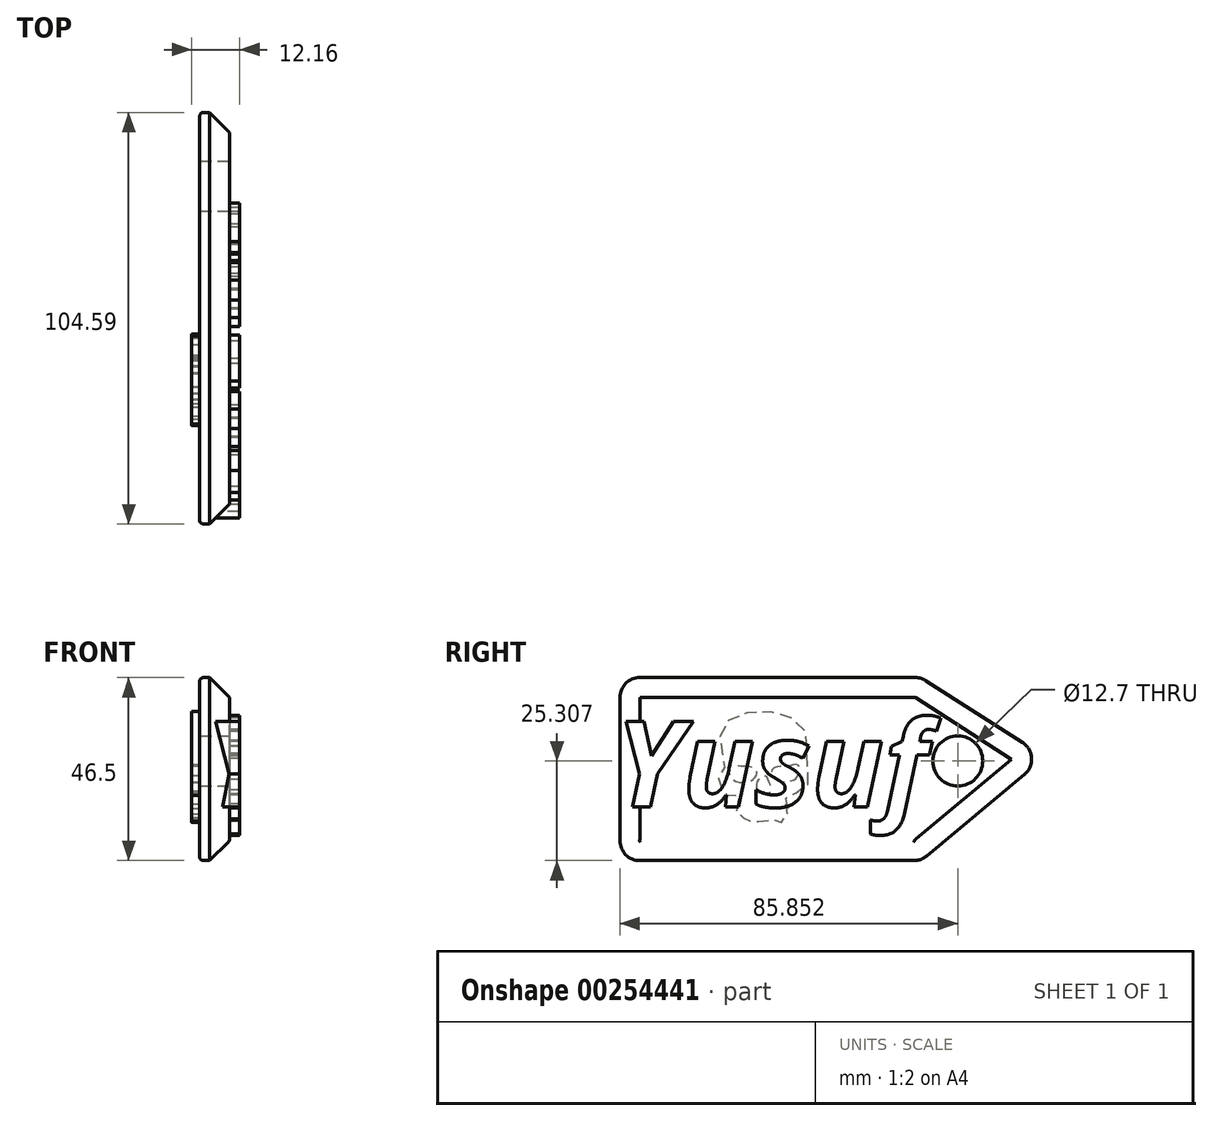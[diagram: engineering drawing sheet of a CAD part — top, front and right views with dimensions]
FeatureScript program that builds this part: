
annotation { "Feature Type Name" : "Feature", "Feature Type Description" : "" }
export const myFeature = defineFeature(function(context is Context, id is Id, definition is map)
    precondition{}
    {
        {
            var Q0;
            Q0=qCreatedBy(makeId("Right.planeOp"),FACE);
            cPlane(context, id + "F0", {"entities" : qUnion([Q0]), "cplaneType" : CPlaneType.OFFSET, "offset" : 25.4 * mm, "width" : 152.4 * mm, "height" : 152.4 * mm});
        }
        {
            var Q0;
            Q0=qCreatedBy(id+"F0.planeOp",FACE);
            var sketch = newSketch(context, id + "F1", { "sketchPlane" : qUnion([Q0])});
            skLineSegment(sketch, "E0", {"start": v(-76.54, 56) * mm, "end": v(-76.54, 9.51) * mm});
            skLineSegment(sketch, "E1", {"start": v(-76.54, 9.51) * mm, "end": v(0, 9.51) * mm});
            skLineSegment(sketch, "E2", {"start": v(-76.54, 56) * mm, "end": v(0, 56) * mm});
            skLineSegment(sketch, "E3", {"start": v(0, 56) * mm, "end": v(0, 9.51) * mm});
            skLineSegment(sketch, "E4", {"start": v(0, 56) * mm, "end": v(31.55, 35.78) * mm});
            skLineSegment(sketch, "E5", {"start": v(31.55, 35.78) * mm, "end": v(0, 9.51) * mm});
            skSolve(sketch);
        }
        {
            var Q0;
            Q0=makeQuery(id+"F1.imprint","IMPRINT",FACE,{"disambiguationData":[TD([[makeQuery(id+"F1.imprint","IMPRINT",EDGE,{"derivedFrom":sQuery(id+"F1.wireOp",EDGE,"E0")}),1.0]])]});
            var Q1;
            Q1=makeQuery(id+"F1.imprint","IMPRINT",FACE,{"disambiguationData":[TD([[makeQuery(id+"F1.imprint","IMPRINT",EDGE,{"derivedFrom":sQuery(id+"F1.wireOp",EDGE,"E3")}),1.0]])]});
            extrude(context, id + "F2", {"entities" : qUnion([Q0, Q1]), "depth" : 7.62 * mm});
        }
        {
            var Q0;
            Q0=makeQuery(id+"F2.opExtrude","CAP_FACE",FACE,{"disambiguationData":[OSD([sQuery(id+"F1.wireOp",EDGE,"E0"),sQuery(id+"F1.wireOp",EDGE,"E1"),sQuery(id+"F1.wireOp",EDGE,"E2"),sQuery(id+"F1.wireOp",EDGE,"E4"),sQuery(id+"F1.wireOp",EDGE,"E5")])],"isStart":false});
            var sketch = newSketch(context, id + "F3", { "sketchPlane" : qUnion([Q0])});
            skPoint(sketch, "E6", {"position": v(9.31, 34.82) * mm});
            skCircle(sketch, "E7", {"center": v(9.31, 34.82) * mm, "radius": 5.77 * mm});
            skSolve(sketch);
        }
        {
            var Q0;
            Q0=sQuery(id+"F3.wireOp",VERTEX,"E6");
            var Q1;
            Q1=makeQuery(id+"F2.opExtrude","SWEPT_BODY",BODY,{"disambiguationData":[OSD([sQuery(id+"F1.wireOp",EDGE,"E0"),sQuery(id+"F1.wireOp",EDGE,"E1"),sQuery(id+"F1.wireOp",EDGE,"E2"),sQuery(id+"F1.wireOp",EDGE,"E4"),sQuery(id+"F1.wireOp",EDGE,"E5")])]});
            hole(context, id + "F4", {"style" : HoleStyle.SIMPLE, "endStyle" : HoleEndStyle.BLIND, "holeDiameter" : 12.7 * mm, "holeDepth" : 25.4 * mm, "tappedDepth" : 12.7 * mm, "tapClearance" : 3, "locations" : qUnion([Q0]), "scope" : qUnion([Q1])});
        }
        {
            var Q0;
            Q0=makeQuery(id+"F2.opExtrude","SWEPT_EDGE",EDGE,{"disambiguationData":[OSD([sQuery(id+"F1.wireOp",EDGE,"E4"),sQuery(id+"F1.wireOp",EDGE,"E5")])]});
            fillet(context, id + "F5", {"entities" : qUnion([Q0]), "radius" : 5.08 * mm, "tangentPropagation" : true, "allowEdgeOverflow" : false});
        }
        {
            var Q0;
            Q0=makeQuery(id+"F2.opExtrude","SWEPT_EDGE",EDGE,{"disambiguationData":[OSD([sQuery(id+"F1.wireOp",EDGE,"E2"),sQuery(id+"F1.wireOp",EDGE,"E3"),sQuery(id+"F1.wireOp",EDGE,"E4")])]});
            fillet(context, id + "F6", {"entities" : qUnion([Q0]), "radius" : 5.08 * mm, "tangentPropagation" : true, "allowEdgeOverflow" : false});
        }
        {
            var Q0;
            Q0=makeQuery(id+"F2.opExtrude","SWEPT_EDGE",EDGE,{"disambiguationData":[OSD([sQuery(id+"F1.wireOp",EDGE,"E0"),sQuery(id+"F1.wireOp",EDGE,"E2")])]});
            fillet(context, id + "F7", {"entities" : qUnion([Q0]), "radius" : 5.08 * mm, "tangentPropagation" : true, "allowEdgeOverflow" : false});
        }
        {
            var Q0;
            Q0=makeQuery(id+"F2.opExtrude","SWEPT_EDGE",EDGE,{"disambiguationData":[OSD([sQuery(id+"F1.wireOp",EDGE,"E0"),sQuery(id+"F1.wireOp",EDGE,"E1")])]});
            var Q1;
            Q1=makeQuery(id+"F2.opExtrude","SWEPT_EDGE",EDGE,{"disambiguationData":[OSD([sQuery(id+"F1.wireOp",EDGE,"E1"),sQuery(id+"F1.wireOp",EDGE,"E3"),sQuery(id+"F1.wireOp",EDGE,"E5")])]});
            fillet(context, id + "F8", {"entities" : qUnion([Q0, Q1]), "radius" : 5.08 * mm, "tangentPropagation" : true, "allowEdgeOverflow" : false});
        }
        {
            var Q0;
            Q0=makeQuery(id+"F2.opExtrude","CAP_FACE",FACE,{"disambiguationData":[OSD([sQuery(id+"F1.wireOp",EDGE,"E0"),sQuery(id+"F1.wireOp",EDGE,"E1"),sQuery(id+"F1.wireOp",EDGE,"E2"),sQuery(id+"F1.wireOp",EDGE,"E4"),sQuery(id+"F1.wireOp",EDGE,"E5")])],"isStart":false});
            var sketch = newSketch(context, id + "F9", { "sketchPlane" : qUnion([Q0])});
            skText(sketch, "E8", { "text": "Yusuf", "fontName": "OpenSans-BoldItalic.ttf"});
            const initialGuessF9  = {"E8": [-0.0778, 0.02318, 1, 0, 0.02187]};
            skSetInitialGuess(sketch, initialGuessF9);
            skSolve(sketch);
        }
        {
            var Q0;
            Q0 = qSketchRegion(id + "F9", true);
            extrude(context, id + "F10", {"entities" : qUnion([Q0]), "operationType" : NewBodyOperationType.ADD, "depth" : 2.54 * mm});
        }
        {
            var Q0;
            Q0=makeQuery(id+"F2.opExtrude","CAP_EDGE",EDGE,{"disambiguationData":[OSD([sQuery(id+"F1.wireOp",EDGE,"E1")])],"isStart":false});
            chamfer(context, id + "F11", {"entities" : qUnion([Q0]), "width" : 5.08 * mm, "tangentPropagation" : true});
        }
        {
            var Q0;
            Q0=makeQuery(id+"F2.opExtrude","CAP_FACE",FACE,{"disambiguationData":[OSD([sQuery(id+"F1.wireOp",EDGE,"E0"),sQuery(id+"F1.wireOp",EDGE,"E1"),sQuery(id+"F1.wireOp",EDGE,"E2"),sQuery(id+"F1.wireOp",EDGE,"E4"),sQuery(id+"F1.wireOp",EDGE,"E5")])],"isStart":true});
            var sketch = newSketch(context, id + "F12", { "sketchPlane" : qUnion([Q0])});
            skFitSpline(sketch, "E9", {"points": [v(29.67, 42.78) * mm, v(31.96, 45.13) * mm, v(34.37, 46.34) * mm, v(37.68, 47.23) * mm, v(42.52, 47.36) * mm, v(45.83, 46.6) * mm, v(48.57, 45.38) * mm, v(50.13, 43.7) * mm, v(51.03, 41.36) * mm, v(50.8, 38.61) * mm, v(50.45, 36.23) * mm, v(50.31, 34.7) * mm, v(50, 33.98) * mm, v(50.18, 32.58) * mm, v(50.67, 31.95) * mm, v(51.44, 30.83) * mm, v(51.44, 29.16) * mm, v(50.54, 26.6) * mm, v(48.78, 26.06) * mm, v(46.8, 26.37) * mm, v(46.08, 25.6) * mm, v(46.17, 24.3) * mm, v(46.98, 21.78) * mm, v(46.62, 21.51) * mm, v(46.08, 21.1) * mm, v(45.27, 20.43) * mm, v(44.95, 20.25) * mm, v(45, 19.58) * mm, v(44.36, 19.44) * mm, v(43.42, 19.58) * mm, v(43.46, 19.98) * mm, v(42.42, 19.71) * mm, v(42.02, 19.53) * mm, v(39.86, 19.58) * mm, v(39.68, 19.71) * mm, v(37.74, 19.85) * mm, v(36.4, 20.34) * mm, v(36.62, 19.49) * mm, v(35.13, 19.35) * mm, v(35.09, 20.16) * mm, v(34.9, 20.61) * mm, v(34.05, 21.33) * mm, v(33.83, 21.74) * mm, v(33.83, 22.77) * mm, v(33.74, 23.5) * mm, v(34.1, 24.26) * mm, v(34.32, 25.16) * mm, v(34.23, 26.1) * mm, v(32.93, 27.05) * mm, v(31.44, 26.55) * mm, v(29.73, 27.32) * mm, v(28.7, 29.2) * mm, v(28.3, 31.23) * mm, v(28.88, 33.08) * mm, v(29.37, 34.11) * mm, v(28.97, 37.4) * mm, v(28.92, 41.18) * mm, v(29.67, 42.78) * mm]});
            skFitSpline(sketch, "E10", {"points": [v(31.13, 33.66) * mm, v(32.8, 33.75) * mm, v(34.28, 33.48) * mm, v(36.4, 33.35) * mm, v(37.88, 32.54) * mm, v(37.97, 31.46) * mm, v(37.11, 30.29) * mm, v(34.6, 29.48) * mm, v(32.07, 30.15) * mm, v(31.3, 31.14) * mm, v(31.13, 33.66) * mm]});
            skFitSpline(sketch, "E11", {"points": [v(43.55, 33.3) * mm, v(46.88, 33.53) * mm, v(48.5, 33.53) * mm, v(49, 33.17) * mm, v(49, 32.13) * mm, v(48.28, 30.56) * mm, v(46.8, 29.57) * mm, v(44.1, 29.48) * mm, v(42.7, 30.15) * mm, v(41.93, 31.05) * mm, v(41.88, 32.5) * mm, v(43.55, 33.3) * mm]});
            skFitSpline(sketch, "E12", {"points": [v(39.81, 31.14) * mm, v(39.05, 30.2) * mm, v(38.55, 29.03) * mm, v(38.33, 27.95) * mm, v(38.55, 26.78) * mm, v(39.18, 26.28) * mm, v(39.81, 26.87) * mm, v(40, 26.91) * mm, v(40.9, 26.37) * mm, v(41.57, 27) * mm, v(41.66, 28.71) * mm, v(41.61, 29.52) * mm, v(39.81, 31.14) * mm]});
            skLineSegment(sketch, "E13", {"start": v(34.46, 23.85) * mm, "end": v(33.83, 22.77) * mm});
            skLineSegment(sketch, "E14", {"start": v(34.46, 23.85) * mm, "end": v(34.05, 21.33) * mm});
            skSolve(sketch);
        }
        {
            var Q0;
            Q0=makeQuery(id+"F12.imprint","IMPRINT",FACE,{"disambiguationData":[TD([[makeQuery(id+"F12.imprint","IMPRINT",EDGE,{"derivedFrom":sQuery(id+"F12.wireOp",EDGE,"E10")}),1.0]])]});
            extrude(context, id + "F13", {"entities" : qUnion([Q0]), "operationType" : NewBodyOperationType.ADD, "depth" : 2 * mm});
        }
        {
            var Q0;
            {var subQ0=sQuery(id+"F1.wireOp",EDGE,"E1");Q0=makeQuery(id+"F11.opChamfer","BLEND_EDGE",EDGE,{"blendedFrom":[makeQuery(id+"F2.opExtrude","CAP_EDGE",EDGE,{"disambiguationData":[OSD([subQ0])],"isStart":false}),makeQuery(id+"F2.opExtrude","CAP_FACE",FACE,{"disambiguationData":[OSD([sQuery(id+"F1.wireOp",EDGE,"E0"),subQ0,sQuery(id+"F1.wireOp",EDGE,"E2"),sQuery(id+"F1.wireOp",EDGE,"E4"),sQuery(id+"F1.wireOp",EDGE,"E5")])],"isStart":false})],"blendedInto":[makeQuery(id+"F2.opExtrude","CAP_FACE",FACE,{"disambiguationData":[OSD([sQuery(id+"F1.wireOp",EDGE,"E0"),subQ0,sQuery(id+"F1.wireOp",EDGE,"E2"),sQuery(id+"F1.wireOp",EDGE,"E4"),sQuery(id+"F1.wireOp",EDGE,"E5")])],"isStart":false})]});}
            var Q1;
            Q1=makeQuery(id+"F4.hole-0.boolean.opBoolean","INTERSECT",EDGE,{"derivedFrom":[makeQuery(id+"F2.opExtrude","CAP_FACE",FACE,{"disambiguationData":[OSD([sQuery(id+"F1.wireOp",EDGE,"E0"),sQuery(id+"F1.wireOp",EDGE,"E1"),sQuery(id+"F1.wireOp",EDGE,"E2"),sQuery(id+"F1.wireOp",EDGE,"E4"),sQuery(id+"F1.wireOp",EDGE,"E5")])],"isStart":true}),makeQuery(id+"F4.hole-0.opRevolve","SWEPT_FACE",FACE,{"disambiguationData":[OSD([sQuery(id+"F4.hole-0.sketch.wireOp",EDGE,"core_line_2")])]})]});
            var Q2;
            Q2=makeQuery(id+"F4.hole-0.boolean.opBoolean","COPY",EDGE,{"derivedFrom":makeQuery(id+"F4.hole-0.opRevolve","SWEPT_EDGE",EDGE,{"disambiguationData":[OSD([sQuery(id+"F4.hole-0.sketch.wireOp",EDGE,"core_line_2"),sQuery(id+"F4.hole-0.sketch.wireOp",EDGE,"core_line_3")])]})});
            var Q3;
            Q3=makeQuery(id+"F2.opExtrude","CAP_EDGE",EDGE,{"disambiguationData":[OSD([sQuery(id+"F1.wireOp",EDGE,"E4")])],"isStart":true});
            fillet(context, id + "F14", {"entities" : qUnion([Q0, Q1, Q2, Q3]), "radius" : 1 * mm, "tangentPropagation" : true, "allowEdgeOverflow" : false});
        }
    });
